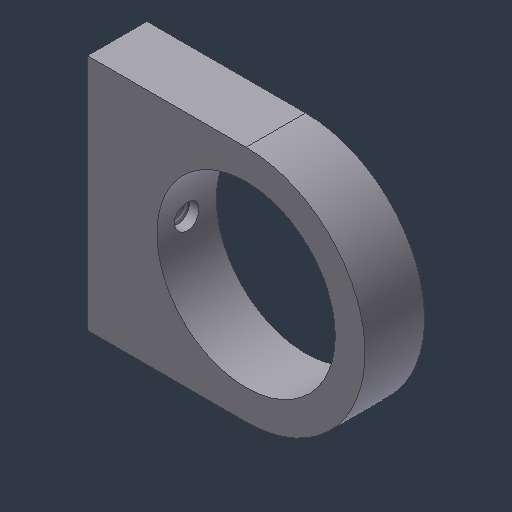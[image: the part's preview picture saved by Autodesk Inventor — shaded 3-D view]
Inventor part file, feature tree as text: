
AUTODESK INVENTOR PART (.ipt)
format: ipt  version: 2024.3 (Build 283343000, 343)  size: 136,704 bytes
history: native  units: mm (DEFAULTED — no unit token found)
features: sketch x3, hole x2, extrude x1
ambient origin geometry x8: Origin, YZ Plane, XZ Plane, XY Plane, X Axis, Y Axis, Z Axis, Center Point
bodies: Solid1 (feature_tree)
feature tree (6):
  extrude  "Extrusion1"  Depth=25.4mm
  hole  "Hole1"  [1 undecoded]
  hole  "Hole2"  [1 undecoded]
  sketch  "Sketch2"  dims[d0=38.1mm d1=25.4mm]
  sketch  "Sketch3"  dims[d2=9.525mm d3=0.0mm d4=44.45mm]
  sketch  "Sketch4"  dims[d5=28.575mm d6=19.05mm d7=9.779mm d8=1.9558mm d9=14.3117mm d10=25.4mm d11=20.594885mm d12=25.4mm d13=3.9624mm d14=9.652mm d15=9.525mm d16=6.35mm d17=14.3117mm d18=13.6144mm d19=20.594885mm]
note: 2 required parameter values undecoded (feature->parameter linkage not recoverable at this tier; creation-order binding heuristic only, values carry confidence <= 0.55)
